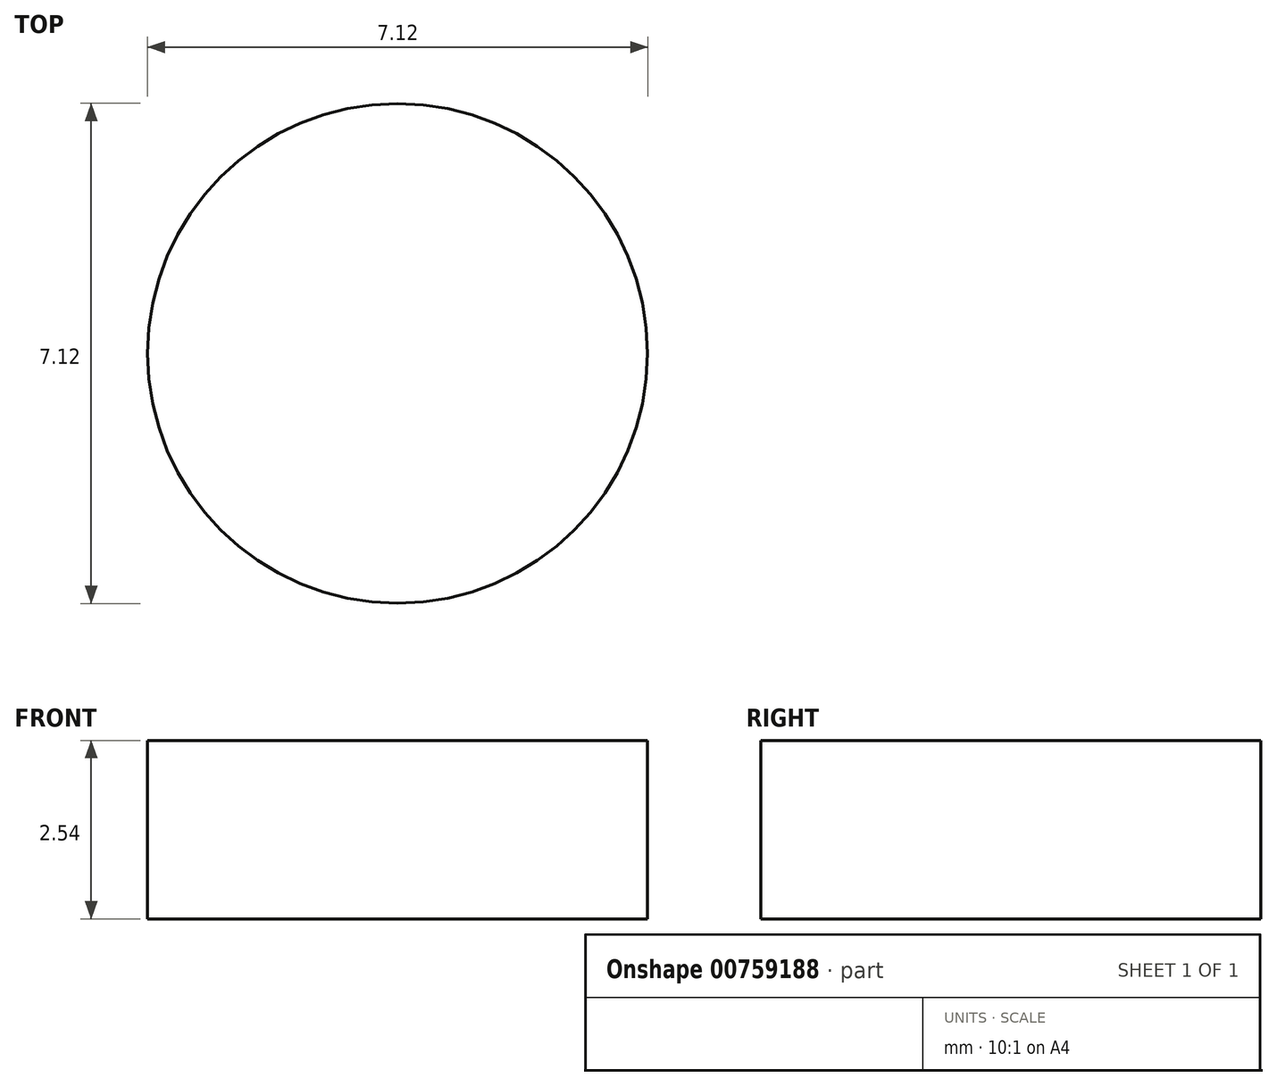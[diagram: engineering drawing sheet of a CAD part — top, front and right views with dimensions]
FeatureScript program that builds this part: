
annotation { "Feature Type Name" : "Feature", "Feature Type Description" : "" }
export const myFeature = defineFeature(function(context is Context, id is Id, definition is map)
    precondition{}
    {
        {
            var Q0;
            Q0=qCreatedBy(makeId("Top.planeOp"),FACE);
            var sketch = newSketch(context, id + "F0", { "sketchPlane" : qUnion([Q0])});
            skCircle(sketch, "E0", {"center": v(0, 0) * mm, "radius": 3.56 * mm});
            skSolve(sketch);
        }
        {
            var Q0;
            Q0=makeQuery(id+"F0.imprint","IMPRINT",FACE,{"disambiguationData":[TD([[makeQuery(id+"F0.imprint","IMPRINT",EDGE,{"derivedFrom":sQuery(id+"F0.wireOp",EDGE,"E0")}),1.0]])]});
            extrude(context, id + "F1", {"entities" : qUnion([Q0]), "depth" : 2.54 * mm, "offsetDistance" : 25.4 * mm});
        }
    });
